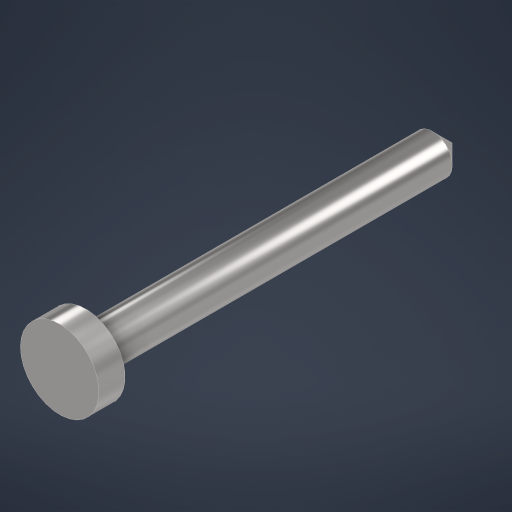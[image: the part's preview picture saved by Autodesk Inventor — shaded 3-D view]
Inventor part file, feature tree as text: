
AUTODESK INVENTOR PART (.ipt)
format: ipt  version: 2023.2 (Build 272271000, 271)  size: 241,152 bytes
history: native  units: mm
features: revolve x1
ambient origin geometry x8: Origin, YZ Plane, XZ Plane, XY Plane, X Axis, Y Axis, Z Axis, Center Point
bodies: Body1 (feature_tree)
feature tree (1):
  revolve  "Revolution1"  [1 undecoded]
note: 1 required parameter value undecoded (feature->parameter linkage not recoverable at this tier; creation-order binding heuristic only, values carry confidence <= 0.55)
